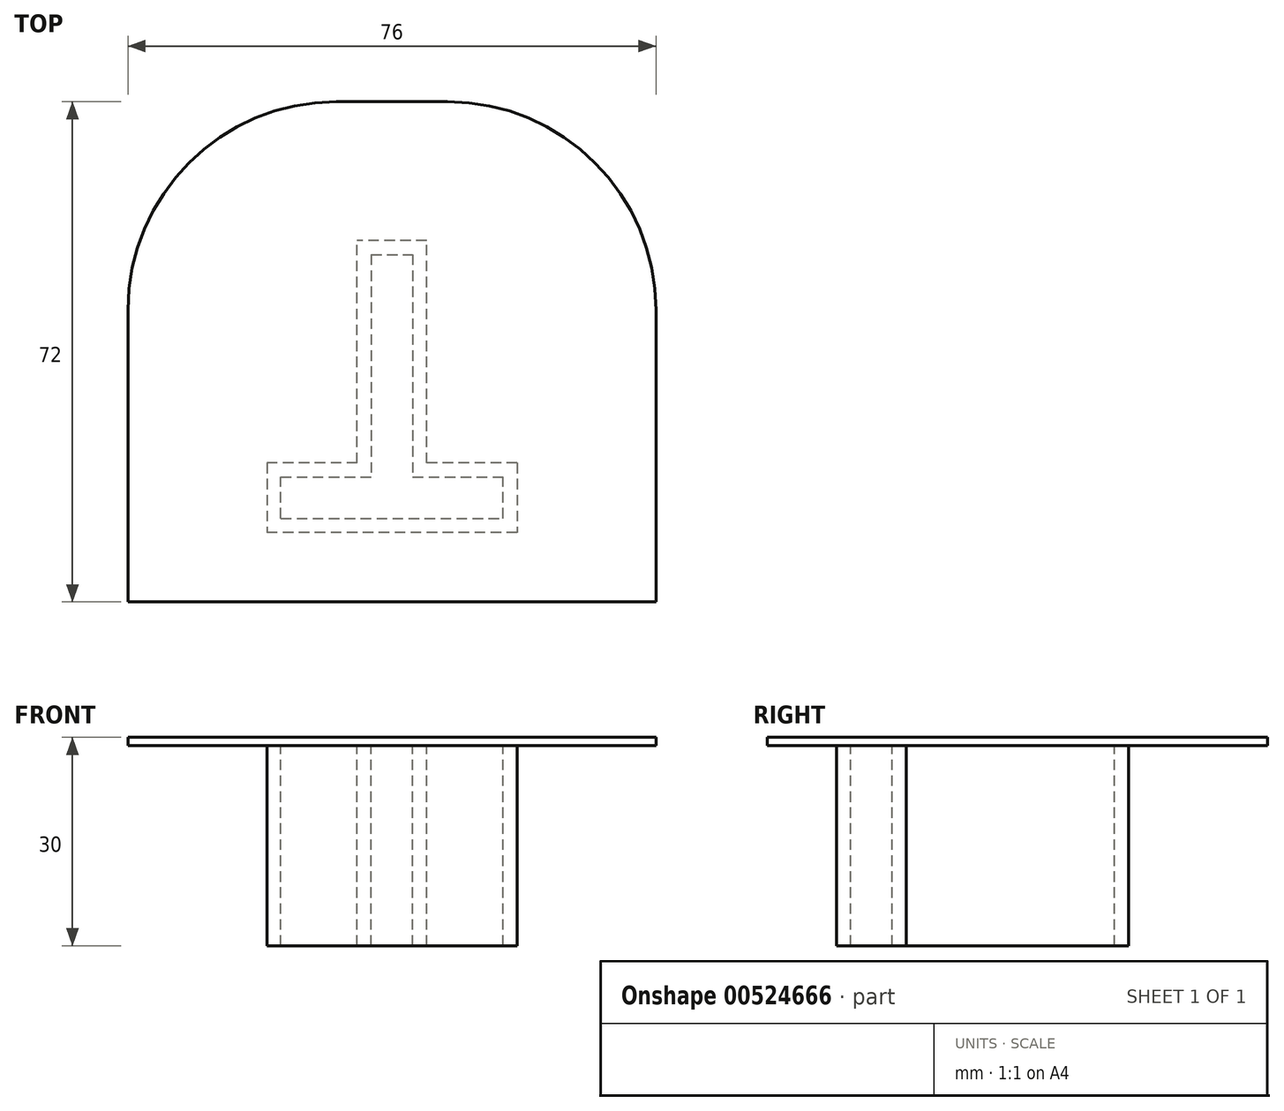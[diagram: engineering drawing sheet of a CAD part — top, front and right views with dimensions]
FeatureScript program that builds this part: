
annotation { "Feature Type Name" : "Feature", "Feature Type Description" : "" }
export const myFeature = defineFeature(function(context is Context, id is Id, definition is map)
    precondition{}
    {
        {
            var Q0;
            Q0=qCreatedBy(makeId("Top.planeOp"),FACE);
            cPlane(context, id + "F0", {"entities" : qUnion([Q0]), "cplaneType" : CPlaneType.OFFSET, "offset" : 30 * mm, "width" : 150 * mm, "height" : 150 * mm});
        }
        {
            var Q0;
            Q0=qCreatedBy(id+"F0.planeOp",FACE);
            var sketch = newSketch(context, id + "F1", { "sketchPlane" : qUnion([Q0])});
            skLineSegment(sketch, "E0.bottom", {"start": v(-38, 0) * mm, "end": v(38, 0) * mm});
            skLineSegment(sketch, "E0.top", {"start": v(-38, 72) * mm, "end": v(38, 72) * mm});
            skLineSegment(sketch, "E0.left", {"start": v(-38, 0) * mm, "end": v(-38, 72) * mm});
            skLineSegment(sketch, "E0.right", {"start": v(38, 0) * mm, "end": v(38, 72) * mm});
            skSolve(sketch);
        }
        {
            var Q0;
            Q0=makeQuery(id+"F1.imprint","IMPRINT",FACE,{"disambiguationData":[TD([[makeQuery(id+"F1.imprint","IMPRINT",EDGE,{"derivedFrom":sQuery(id+"F1.wireOp",EDGE,"E0.bottom")}),1.0]])]});
            extrude(context, id + "F2", {"entities" : qUnion([Q0]), "oppositeDirection" : true, "depth" : 1.2 * mm, "offsetDistance" : 25 * mm});
        }
        {
            var Q0;
            Q0=makeQuery(id+"F2.opExtrude","SWEPT_EDGE",EDGE,{"disambiguationData":[OSD([sQuery(id+"F1.wireOp",EDGE,"E0.top"),sQuery(id+"F1.wireOp",EDGE,"E0.left")])]});
            var Q1;
            Q1=makeQuery(id+"F2.opExtrude","SWEPT_EDGE",EDGE,{"disambiguationData":[OSD([sQuery(id+"F1.wireOp",EDGE,"E0.top"),sQuery(id+"F1.wireOp",EDGE,"E0.right")])]});
            fillet(context, id + "F3", {"entities" : qUnion([Q0, Q1]), "radius" : 30 * mm, "tangentPropagation" : true, "allowEdgeOverflow" : false});
        }
        {
            var Q0;
            Q0=makeQuery(id+"F2.opExtrude","CAP_FACE",FACE,{"disambiguationData":[OSD([sQuery(id+"F1.wireOp",EDGE,"E0.bottom"),sQuery(id+"F1.wireOp",EDGE,"E0.top"),sQuery(id+"F1.wireOp",EDGE,"E0.left"),sQuery(id+"F1.wireOp",EDGE,"E0.right")])],"isStart":false});
            var sketch = newSketch(context, id + "F4", { "sketchPlane" : qUnion([Q0])});
            skLineSegment(sketch, "E1.bottom", {"start": v(18, -20) * mm, "end": v(5, -20) * mm});
            skLineSegment(sketch, "E1.top", {"start": v(18, -10) * mm, "end": v(-18, -10) * mm});
            skLineSegment(sketch, "E1.left", {"start": v(18, -20) * mm, "end": v(18, -10) * mm});
            skLineSegment(sketch, "E1.right", {"start": v(-18, -20) * mm, "end": v(-18, -10) * mm});
            skLineSegment(sketch, "E2.top", {"start": v(5, -52) * mm, "end": v(-5, -52) * mm});
            skLineSegment(sketch, "E2.left", {"start": v(5, -20) * mm, "end": v(5, -52) * mm});
            skLineSegment(sketch, "E2.right", {"start": v(-5, -20) * mm, "end": v(-5, -52) * mm});
            skLineSegment(sketch, "E3.trimOffspring", {"start": v(-5, -20) * mm, "end": v(-18, -20) * mm});
            skLineSegment(sketch, "E4.0", {"start": v(3, -50) * mm, "end": v(-3, -50) * mm});
            skLineSegment(sketch, "E5.0", {"start": v(3, -18) * mm, "end": v(3, -50) * mm});
            skLineSegment(sketch, "E6.0", {"start": v(-3, -18) * mm, "end": v(-3, -50) * mm});
            skLineSegment(sketch, "E7.0", {"start": v(16, -18) * mm, "end": v(3, -18) * mm});
            skLineSegment(sketch, "E8.0", {"start": v(16, -18) * mm, "end": v(16, -12) * mm});
            skLineSegment(sketch, "E9.0", {"start": v(16, -12) * mm, "end": v(-16, -12) * mm});
            skLineSegment(sketch, "E10.0", {"start": v(-16, -18) * mm, "end": v(-16, -12) * mm});
            skLineSegment(sketch, "E11.0", {"start": v(-3, -18) * mm, "end": v(-16, -18) * mm});
            skSolve(sketch);
        }
        {
            var Q0;
            Q0=makeQuery(id+"F4.imprint","IMPRINT",FACE,{"disambiguationData":[TD([[makeQuery(id+"F4.imprint","IMPRINT",EDGE,{"derivedFrom":sQuery(id+"F4.wireOp",EDGE,"E1.bottom")}),-1.0]])]});
            var Q1;
            Q1=qCreatedBy(makeId("Top.planeOp"),FACE);
            extrude(context, id + "F5", {"entities" : qUnion([Q0]), "operationType" : NewBodyOperationType.ADD, "endBound" : BoundingType.UP_TO_SURFACE, "depth" : 25 * mm, "endBoundEntityFace" : qUnion([Q1]), "offsetDistance" : 25 * mm});
        }
    });
